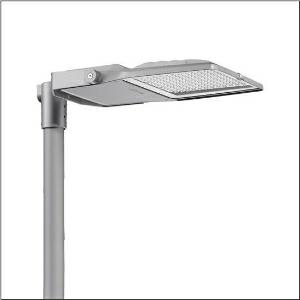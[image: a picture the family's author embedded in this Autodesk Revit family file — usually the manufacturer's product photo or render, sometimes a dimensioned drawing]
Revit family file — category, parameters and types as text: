
# Revit family: floodlight_fl_21_iq_midi___pl61_5xa7781e2c3a_352e
name_source: partatom
category: Lighting Fixtures
units: mm (PartAtom-declared; Revit-internal decimal feet)

## family parameters
Cut with Voids When Loaded = No
Host = Face
Light Source = No
Part Type = Normal
Room Calculation Point = No
Round Connector Dimension = Use Diameter
Shared = No

## types (1)
- --- (1 x LED, 26360 lm, 208.1 W, 3000K)
    Apparent Load = 208 VA
    CIE Flux Codes = 33 65 98 100 100
    Color Rendering = 70
    Color Temperature = 3000K
    Default Elevation = 1800 mm
    Description = Floodlight FL 21 iQ midi, floodlight, primary light control with lens, of PMMA, primary optical cover: protective disc, of toughened safety glass, transparent, light distribution: PL61, light emission: direct distribution, installation type: surface-mounted, lamps: LED, High Power LED, rated values: 26.360lm | 208,1W | 126,7lm/W (begin service life); end service life: 26.360lm | 227,1W; at 50% lumin. flux: 13.180lm | 90,1W | 146,3lm/W, colour temperature: 3000K, colour rendering: CRI > 70, light colour: 730, light setting 1 begin service life: 100% | 26.360lm | 208,1W | 126,7lm/W | 3.000K, light setting 1 end service life: 227,1W, further light settings possible, control: optimised constant luminous flux control (CLO 2.0), Desk-Remote (wireless, voltage-free reading and setting of iQ features in the workshop via application-optimized NFC function/RFID function), Light-Fading, Smart-Wire, Night-Set, Lumen-Switch, Temp-Guard, Auto-Match, pre-setting: linear dimming characteristic, with terminal, 6-pole, mains connection: 220..240V, AC, 50/60Hz, luminaire housing, of diecast aluminium, powder-coated, SITECO metallic grey (DB 702S), corrosivity category C5 mid according to DIN EN ISO 12944suitable for swimming poolschlorine-resistant, sealing non-destructively replaceable, please order mast flange separately, mast bracket, of steel, galvanised, powder-coated, SITECO metallic grey (DB 702S), protection rating (complete): IP66, insulation class (complete): insulation class II (safety insulation), certification: CE, ENEC, VDE, protection symbol: D, impact resistance: IK08, permissible operating ambient temperature: -40..+40°C, permissible operating ambient temperature for outdoor applications: -40..+50°C, standard: DIN EN 12944, LABS conformity tested according to VDMA 24364:2018-05, packaging unit: 1 piece

Light Distribution: PL61
    Height = 76 mm
    Lamp = 1 x LED
    Lamp Light Flux = 26360 lm
    Lamp Power = 208.1 W
    Lamp count = 1
    Length = 657 mm
    Luminous efficacy = 127 lm/W
    Manufacturer = Siteco
    ModVariant = No
    Model = 5XA7781E2C3A
    Number of Poles = 1
    OnlyDefault = Yes
    Power Factor = 1
    Product Name = Floodlight FL 21 iQ midi | PL61
    Product group = floodlight | pylon annexe
    ProductGroupID = 6201
    Protection Class = Protection class II
    Protection Degree = IP 66
    RLX_Detail_Level = 1
    RLX_Emergency_Light_Flux = 0 lm
    RLX_Emergency_Type = 0
    RLX_Emergency_Type_DB = No
    RlxData = <blob elided: 154049 chars, md5=2feec78f>
    Socket = socket
    Standby Power = 0 W
    System Light Flux = 26360 lm
    System Power = 208 W
    Type Comments = factory setting: luminous flux: 100 % | dim-lin: 254 | 710 mA
    Type Image = l_1007123.jpg
    URL = http://relux.com
    VarID = @adj_108883
    Voltage = 0 V
    Weight = 0.00 kg
    Width = 442 mm

## geometry (parser evidence)
native form markers: Blend x4, Sweep x13
no freeform markers — native parametric forms only
